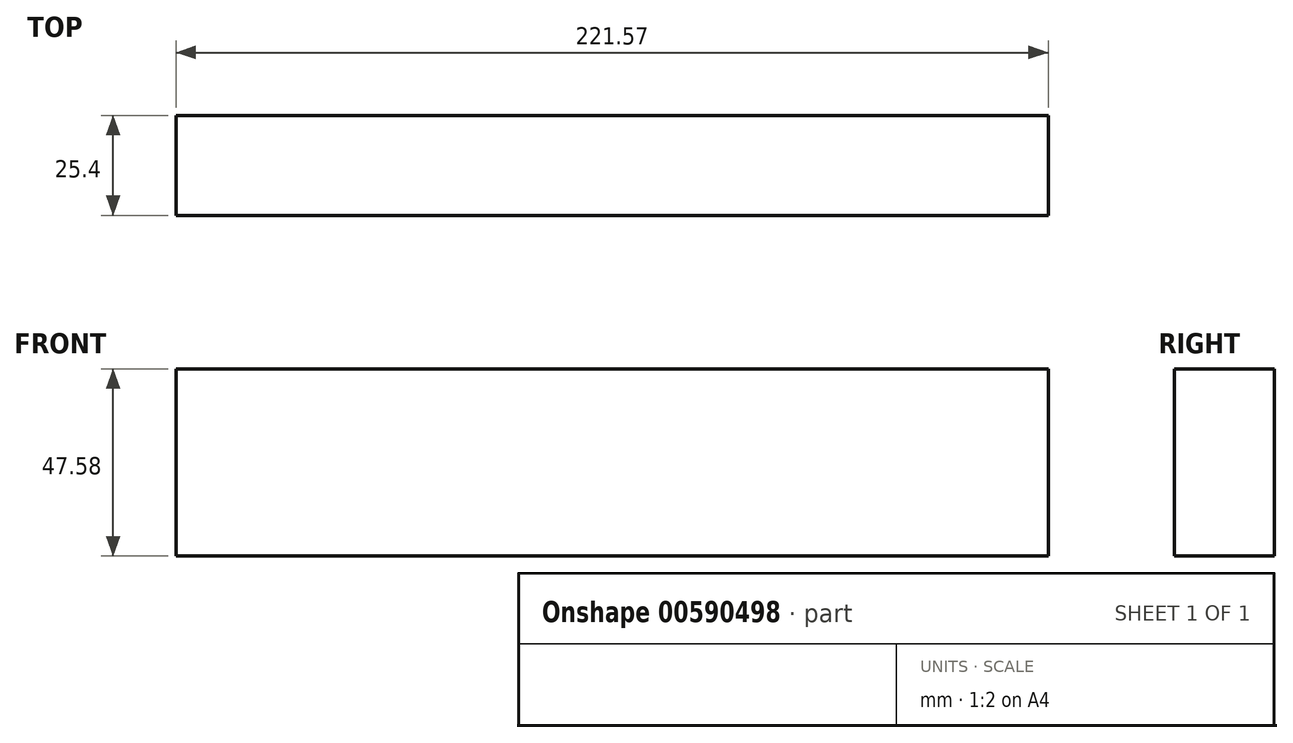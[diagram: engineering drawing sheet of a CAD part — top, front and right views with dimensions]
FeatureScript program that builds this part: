
annotation { "Feature Type Name" : "Feature", "Feature Type Description" : "" }
export const myFeature = defineFeature(function(context is Context, id is Id, definition is map)
    precondition{}
    {
        {
            var Q0;
            Q0=qCreatedBy(makeId("Front.planeOp"),FACE);
            var sketch = newSketch(context, id + "F0", { "sketchPlane" : qUnion([Q0])});
            skLineSegment(sketch, "E0.bottom", {"start": v(-86, 28.84) * mm, "end": v(135.57, 28.84) * mm});
            skLineSegment(sketch, "E0.top", {"start": v(-86, 76.42) * mm, "end": v(135.57, 76.42) * mm});
            skLineSegment(sketch, "E0.left", {"start": v(-86, 28.84) * mm, "end": v(-86, 76.42) * mm});
            skLineSegment(sketch, "E0.right", {"start": v(135.57, 28.84) * mm, "end": v(135.57, 76.42) * mm});
            skSolve(sketch);
        }
        {
            var Q0;
            Q0 = qSketchRegion(id + "F0", true);
            extrude(context, id + "F1", {"entities" : qUnion([Q0]), "depth" : 25.4 * mm, "offsetDistance" : 25.4 * mm});
        }
    });
